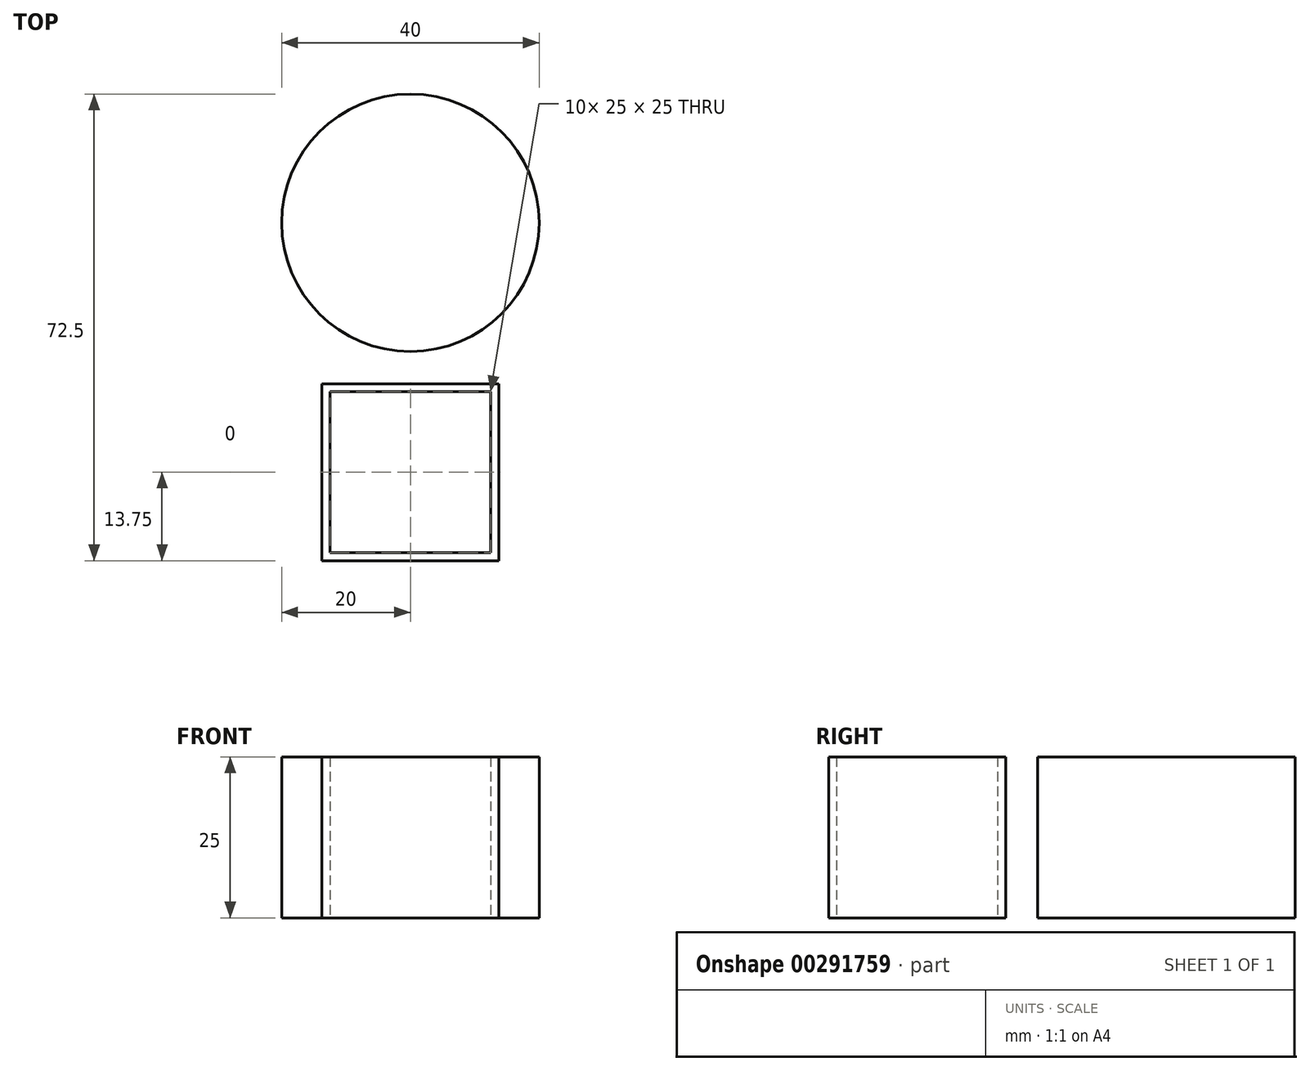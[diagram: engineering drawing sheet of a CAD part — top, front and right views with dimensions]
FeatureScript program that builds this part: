
annotation { "Feature Type Name" : "Feature", "Feature Type Description" : "" }
export const myFeature = defineFeature(function(context is Context, id is Id, definition is map)
    precondition{}
    {
        {
            var Q0;
            Q0=qCreatedBy(makeId("Top.planeOp"),FACE);
            var sketch = newSketch(context, id + "F0", { "sketchPlane" : qUnion([Q0])});
            skLineSegment(sketch, "E0.bottom", {"start": v(12.5, 12.5) * mm, "end": v(-12.5, 12.5) * mm});
            skLineSegment(sketch, "E0.top", {"start": v(12.5, -12.5) * mm, "end": v(-12.5, -12.5) * mm});
            skLineSegment(sketch, "E0.left", {"start": v(12.5, 12.5) * mm, "end": v(12.5, -12.5) * mm});
            skLineSegment(sketch, "E0.right", {"start": v(-12.5, 12.5) * mm, "end": v(-12.5, -12.5) * mm});
            skPoint(sketch, "E0.middle", {"position": v(0, 0) * mm});
            skLineSegment(sketch, "E1.bottom", {"start": v(13.75, 13.75) * mm, "end": v(-13.75, 13.75) * mm});
            skLineSegment(sketch, "E1.top", {"start": v(13.75, -13.75) * mm, "end": v(-13.75, -13.75) * mm});
            skLineSegment(sketch, "E1.left", {"start": v(13.75, 13.75) * mm, "end": v(13.75, -13.75) * mm});
            skLineSegment(sketch, "E1.right", {"start": v(-13.75, 13.75) * mm, "end": v(-13.75, -13.75) * mm});
            skCircle(sketch, "E2", {"center": v(0, 38.75) * mm, "radius": 20 * mm});
            skLineSegment(sketch, "E3", {"start": v(0, 58.75) * mm, "end": v(68.44, 58.75) * mm});
            skSolve(sketch);
        }
        {
            var Q0;
            Q0=makeQuery(id+"F0.imprint","IMPRINT",FACE,{"disambiguationData":[TD([[makeQuery(id+"F0.imprint","IMPRINT",EDGE,{"derivedFrom":sQuery(id+"F0.wireOp",EDGE,"E2")}),1.0]])]});
            var Q1;
            Q1=makeQuery(id+"F0.imprint","IMPRINT",FACE,{"disambiguationData":[TD([[makeQuery(id+"F0.imprint","IMPRINT",EDGE,{"derivedFrom":sQuery(id+"F0.wireOp",EDGE,"E0.bottom")}),-1.0]])]});
            extrude(context, id + "F1", {"entities" : qUnion([Q0, Q1]), "depth" : 25 * mm});
        }
    });
